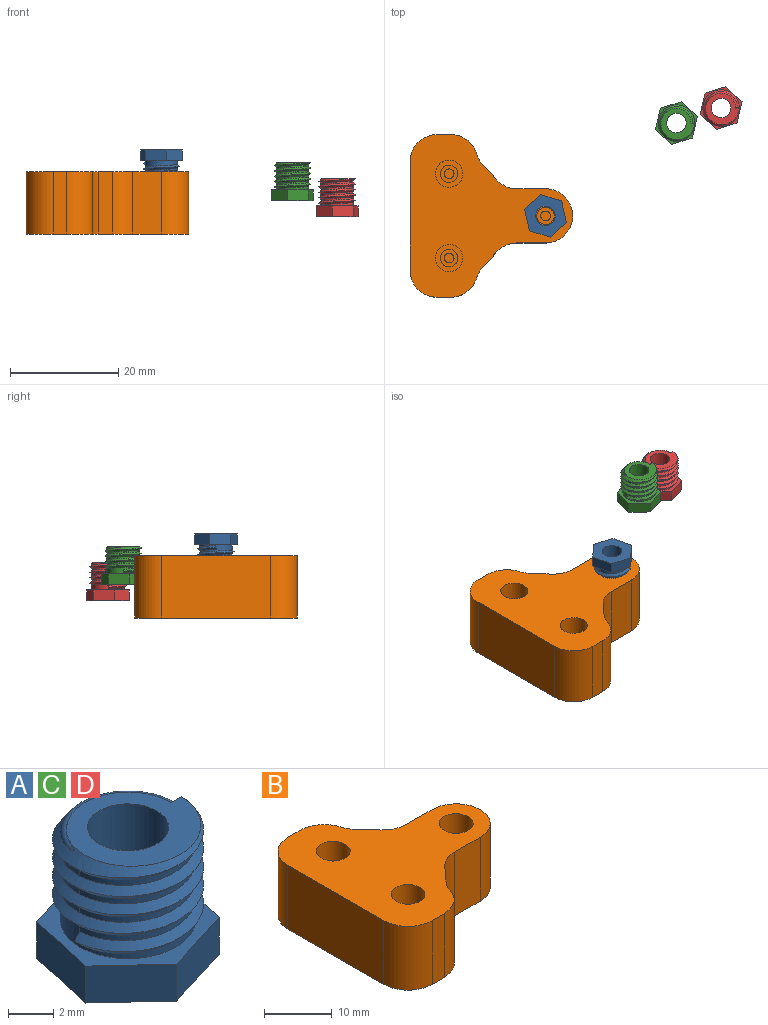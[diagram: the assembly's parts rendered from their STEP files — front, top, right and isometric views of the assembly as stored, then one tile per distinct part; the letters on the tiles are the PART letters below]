
ASSEMBLY  parts=4 mates=1
PART A: 20 faces, bbox 7.7x7.9x7.7 mm
  f0: plane 0.66x0.36mm, normal (0,1,0.05), area 0.1mm2, adj f6,f8,f10,f19
  f1: bspline ~7.74x6.7mm, area 43.3mm2, adj f3,f4,f5,f6,f8,f9,f10,f19
  f2: cylinder r=3mm len=6mm, axis (0,0,-1), area 12.3mm2, adj f3,f9,f10,f18
  f3: cylinder r=3mm len=6mm, axis (0,0,-1), area 5.7mm2, adj f1,f2,f4,f10
  f4: cylinder r=3mm len=6mm, axis (0,0,-1), area 5.7mm2, adj f1,f3,f5,f10
  f5: cylinder r=3mm len=6mm, axis (0,0,-1), area 5.7mm2, adj f1,f4,f6,f10
  f6: cylinder r=3mm len=6mm, axis (0,0,-1), area 4mm2, adj f0,f1,f5,f10,f19
  f7: cylinder r=1.8mm len=7mm, axis (0,0,-1), area 79.2mm2, adj f8,f17
  f8: plane 6.21x5.81mm, normal (0,0,1), area 16.6mm2, adj f0,f1,f7,f19
  f9: plane 0.7x0.35mm, normal (0,1,-0.05), area 0.1mm2, adj f1,f2,f10
  f10: bspline ~6.7x6.65mm, area 44.6mm2, adj f0,f1,f2,f3,f4,f5,f6,f9
  f11: plane 3.94x2mm, normal (-0.98,0.22,0), area 8.1mm2, adj f12,f16,f17,f18
  f12: plane 3.86x2mm, normal (-0.3,0.96,0), area 8.1mm2, adj f11,f13,f17,f18
  f13: plane 2.96x2.75mm, normal (0.68,0.73,0), area 8.1mm2, adj f12,f14,f17,f18
  f14: plane 3.94x2mm, normal (0.98,-0.22,0), area 8.1mm2, adj f13,f15,f17,f18
  f15: plane 3.86x2mm, normal (0.3,-0.96,0), area 8.1mm2, adj f14,f16,f17,f18
  f16: plane 2.96x2.75mm, normal (-0.68,-0.73,0), area 8.1mm2, adj f11,f15,f17,f18
  f17: plane 7.88x7.72mm, normal (0,0,-1), area 32.3mm2, adj f7,f11,f12,f13,f14,f15,f16
  f18: plane 7.88x7.72mm, normal (0,0,1), area 14.2mm2, adj f2,f11,f12,f13,f14,f15,f16
  f19: torus R=2.7mm, axis (0,0,1), area 3.5mm2, adj f0,f1,f6,f8
PART B: 44 faces, bbox 30x30x11.5 mm
  f0: plane 30x30mm, normal (0,0,1), area 488.2mm2, adj f2,f26,f27,f28,f29,f30,f31,f32
  f1: plane 30x30mm, normal (0,0,-1), area 547.1mm2, adj f2,f29,f30,f31,f32,f33,f34,f35
  f2: plane 11.5x2.53mm, normal (0,1,0), area 29mm2, adj f0,f1,f31,f38
  f3: plane 5x5mm, normal (0,0,1), area 11.6mm2, adj f24,f28
  f4: plane 5x5mm, normal (0,0,1), area 11.6mm2, adj f22,f27
  f5: plane 5x5mm, normal (0,0,1), area 11.6mm2, adj f20,f26
  f6: cylinder r=0.9mm len=2.5mm, axis (0,0,-1), area 9.9mm2, adj f9,f10,f11,f19,f23
  f7: cylinder r=0.9mm len=2.5mm, axis (0,0,-1), area 9.9mm2, adj f9,f10,f13,f14,f25
  f8: cylinder r=0.9mm len=2.5mm, axis (0,0,-1), area 9.9mm2, adj f9,f10,f16,f17,f21
  f9: plane 18.41x16.83mm, normal (0,0,-1), area 52.6mm2, adj f6,f7,f8,f11,f12,f13,f14,f15
  f10: plane 19.58x17.36mm, normal (0,0,1), area 60.2mm2, adj f6,f7,f8,f11,f12,f13,f14,f15
  f11: plane 6.43x6.43mm, normal (0.71,0.71,0), area 13.6mm2, adj f6,f9,f10,f12
  f12: cylinder r=1mm len=1.5mm, axis (0,0,1), area 2.4mm2, adj f9,f10,f11,f13
  f13: plane 6.43x6.43mm, normal (0.71,-0.71,0), area 13.6mm2, adj f7,f9,f10,f12
  f14: plane 7.22x7.22mm, normal (-0.71,0.71,0), area 15.3mm2, adj f7,f9,f10,f15
  f15: cylinder r=1mm len=1.5mm, axis (0,0,-1), area 1.2mm2, adj f9,f10,f14,f16
  f16: plane 9.21x1.5mm, normal (0,1,0), area 13.8mm2, adj f8,f9,f10,f15
  f17: plane 9.21x1.5mm, normal (0,-1,0), area 13.8mm2, adj f8,f9,f10,f18
  f18: cylinder r=1mm len=1.5mm, axis (0,0,-1), area 1.2mm2, adj f9,f10,f17,f19
  f19: plane 7.22x7.22mm, normal (-0.71,-0.71,0), area 15.3mm2, adj f6,f9,f10,f18
  f20: cylinder r=1.6mm len=3.2mm, axis (0,0,1), area 30.2mm2, adj f5,f21
  f21: plane 3.2x3.2mm, normal (0,0,1), area 5.5mm2, adj f8,f20
  f22: cylinder r=1.6mm len=3.2mm, axis (0,0,1), area 30.2mm2, adj f4,f23
  f23: plane 3.2x3.2mm, normal (0,0,1), area 5.5mm2, adj f6,f22
  f24: cylinder r=1.6mm len=3.2mm, axis (0,0,1), area 30.2mm2, adj f3,f25
  f25: plane 3.2x3.2mm, normal (0,0,1), area 5.5mm2, adj f7,f24
  f26: cylinder r=2.5mm len=5mm, axis (0,0,-1), area 78.5mm2, adj f0,f5
  f27: cylinder r=2.5mm len=5mm, axis (0,0,-1), area 78.5mm2, adj f0,f4
  f28: cylinder r=2.5mm len=5mm, axis (0,0,-1), area 78.5mm2, adj f0,f3
  f29: plane 11.5x2.53mm, normal (0,-1,0), area 29mm2, adj f0,f1,f32,f37
  f30: plane 20x11.5mm, normal (-1,0,0), area 230mm2, adj f0,f1,f31,f32
  f31: cylinder r=5mm len=11.5mm, axis (0,0,-1), area 90.3mm2, adj f0,f1,f2,f30
  f32: cylinder r=5mm len=11.5mm, axis (0,0,1), area 90.3mm2, adj f0,f1,f29,f30
  f33: plane 11.5x2.87mm, normal (0.74,-0.67,0), area 44.6mm2, adj f0,f1,f39,f41
  f34: plane 11.5x5.29mm, normal (0,-1,0), area 60.8mm2, adj f0,f1,f39,f43
  f35: plane 11.5x2.87mm, normal (0.74,0.67,0), area 44.6mm2, adj f0,f1,f40,f42
  f36: plane 11.5x5.29mm, normal (0,1,0), area 60.8mm2, adj f0,f1,f40,f43
  f37: cylinder r=5mm len=11.5mm, axis (0,0,1), area 73.6mm2, adj f0,f1,f29,f41
  f38: cylinder r=5mm len=11.5mm, axis (0,0,-1), area 73.6mm2, adj f0,f1,f2,f42
  f39: cylinder r=5mm len=11.5mm, axis (0,0,-1), area 47.9mm2, adj f0,f1,f33,f34
  f40: cylinder r=5mm len=11.5mm, axis (0,0,-1), area 47.9mm2, adj f0,f1,f35,f36
  f41: cylinder r=5mm len=11.5mm, axis (0,0,1), area 25.7mm2, adj f0,f1,f33,f37
  f42: cylinder r=5mm len=11.5mm, axis (0,0,-1), area 25.7mm2, adj f0,f1,f35,f38
  f43: cylinder r=5mm len=11.5mm, axis (0,0,-1), area 180.6mm2, adj f0,f1,f34,f36
PART C: same geometry as A
PART D: same geometry as A
PLACE A rot(axis=(1,0,0),180deg) t=(-27.42,-17.44,7.02)mm
PLACE B t=(-37.42,-17.44,-6.48)mm
PLACE C t=(-3.26,-0.32,1.68)mm
PLACE D t=(4.97,2.46,-1.28)mm
MATE fastened A.f7 <-> B.f26  axis (0,0,-1) through (-27.42,-17.44,2.02)mm
